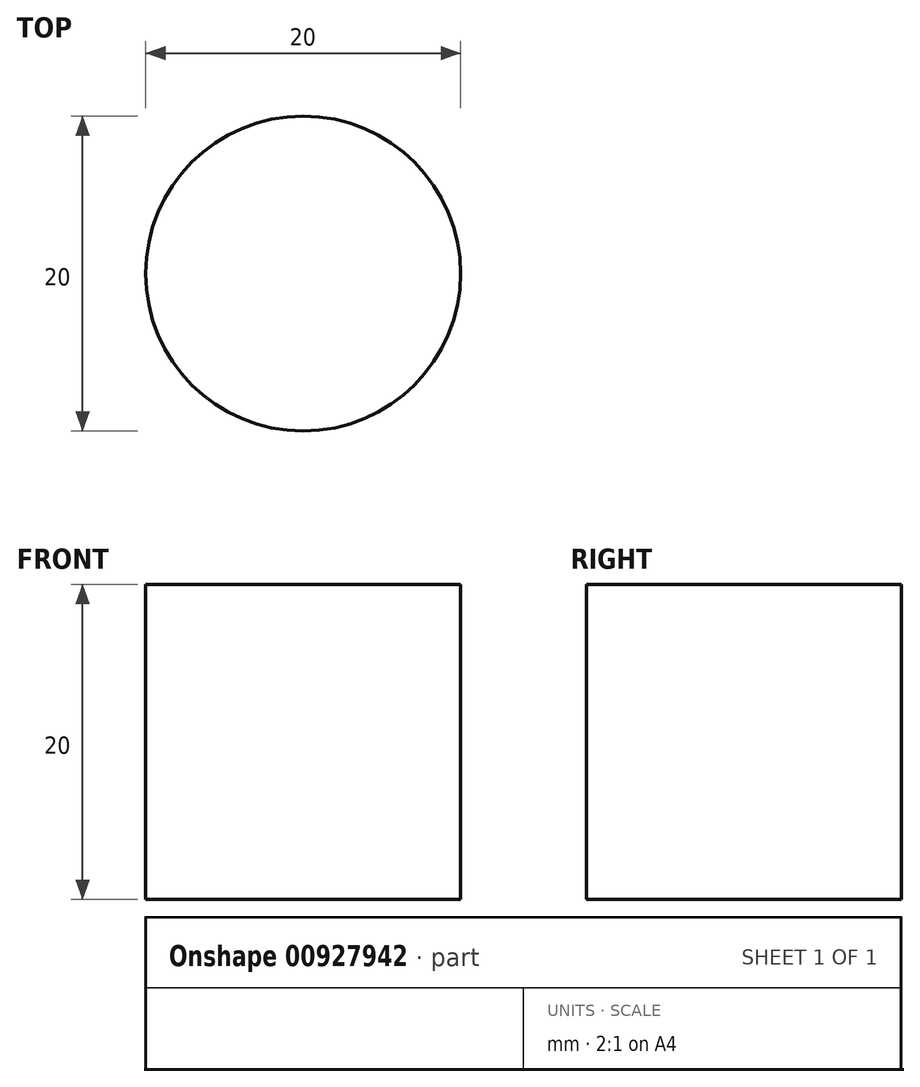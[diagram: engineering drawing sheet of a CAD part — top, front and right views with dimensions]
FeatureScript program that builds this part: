
annotation { "Feature Type Name" : "Feature", "Feature Type Description" : "" }
export const myFeature = defineFeature(function(context is Context, id is Id, definition is map)
    precondition{}
    {
        {
            var Q0;
            Q0=qCreatedBy(makeId("Top.planeOp"),FACE);
            var sketch = newSketch(context, id + "F0", { "sketchPlane" : qUnion([Q0])});
            skCircle(sketch, "E0", {"center": v(0, 0) * mm, "radius": 10 * mm});
            skSolve(sketch);
        }
        {
            var Q0;
            Q0 = qSketchRegion(id + "F0", true);
            extrude(context, id + "F1", {"entities" : qUnion([Q0]), "depth" : 20 * mm, "offsetDistance" : 25 * mm});
        }
    });
